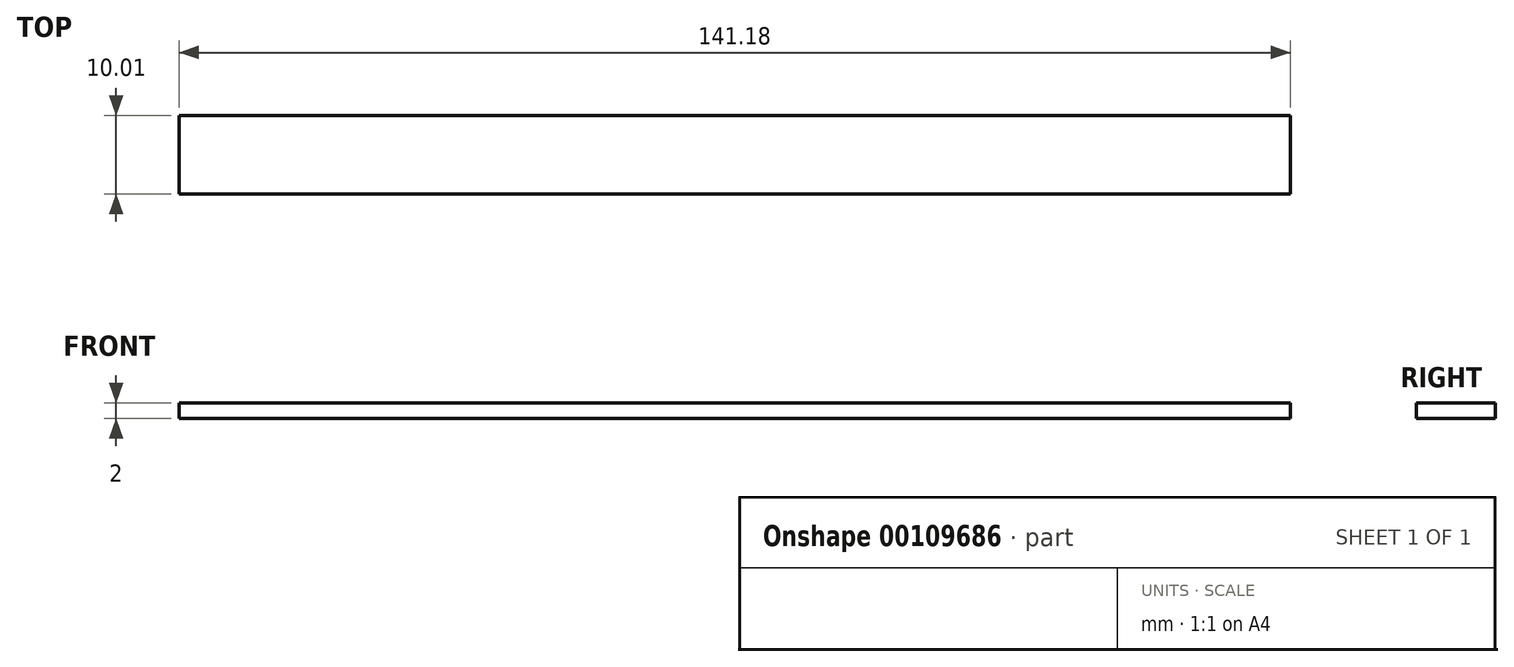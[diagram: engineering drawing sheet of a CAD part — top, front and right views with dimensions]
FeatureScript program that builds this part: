
annotation { "Feature Type Name" : "Feature", "Feature Type Description" : "" }
export const myFeature = defineFeature(function(context is Context, id is Id, definition is map)
    precondition{}
    {
        {
            var Q0;
            Q0=qCreatedBy(makeId("Top.planeOp"),FACE);
            var sketch = newSketch(context, id + "F0", { "sketchPlane" : qUnion([Q0])});
            skLineSegment(sketch, "E0.bottom", {"start": v(-72.9, 6.21) * mm, "end": v(68.27, 6.21) * mm});
            skLineSegment(sketch, "E0.top", {"start": v(-72.9, -3.8) * mm, "end": v(68.27, -3.8) * mm});
            skLineSegment(sketch, "E0.left", {"start": v(-72.9, 6.21) * mm, "end": v(-72.9, -3.8) * mm});
            skLineSegment(sketch, "E0.right", {"start": v(68.27, 6.21) * mm, "end": v(68.27, -3.8) * mm});
            skSolve(sketch);
        }
        {
            var Q0;
            Q0=makeQuery(id+"F0.imprint","IMPRINT",FACE,{"disambiguationData":[TD([[makeQuery(id+"F0.imprint","IMPRINT",EDGE,{"derivedFrom":sQuery(id+"F0.wireOp",EDGE,"E0.bottom")}),-1.0]])]});
            extrude(context, id + "F1", {"entities" : qUnion([Q0]), "depth" : 2 * mm});
        }
    });
